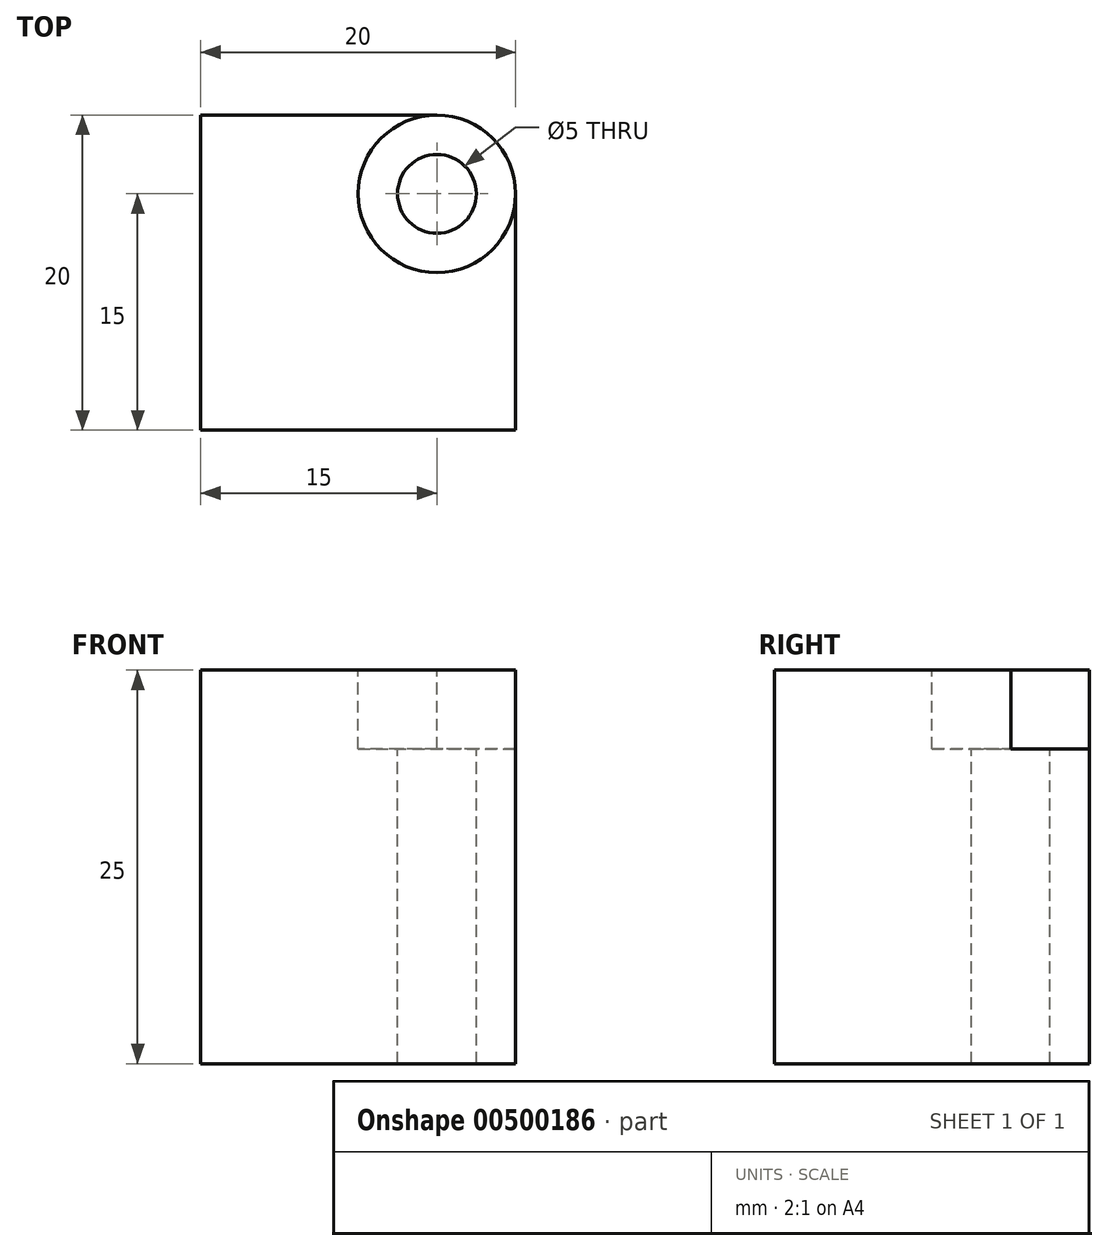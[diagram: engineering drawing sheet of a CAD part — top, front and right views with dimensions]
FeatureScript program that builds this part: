
annotation { "Feature Type Name" : "Feature", "Feature Type Description" : "" }
export const myFeature = defineFeature(function(context is Context, id is Id, definition is map)
    precondition{}
    {
        {
            var Q0;
            Q0=qCreatedBy(makeId("Top.planeOp"),FACE);
            var sketch = newSketch(context, id + "F0", { "sketchPlane" : qUnion([Q0])});
            skLineSegment(sketch, "E0", {"start": v(-68, 40) * mm, "end": v(-68, 20) * mm});
            skLineSegment(sketch, "E1", {"start": v(-68, 20) * mm, "end": v(-48, 20) * mm});
            skLineSegment(sketch, "E2", {"start": v(-68, 40) * mm, "end": v(-53, 40) * mm});
            skLineSegment(sketch, "E3", {"start": v(-48, 35) * mm, "end": v(-48, 20) * mm});
            skLineSegment(sketch, "E4", {"start": v(0, 20) * mm, "end": v(44, 20) * mm});
            skPoint(sketch, "E5.visualSharp", {"position": v(-48, 40) * mm});
            skArc(sketch, "E5.filletArc", {"start": v(-48, 35) * mm, "mid": v(-49.46, 38.54) * mm, "end": v(-53, 40) * mm});
            skSolve(sketch);
        }
        {
            var Q0;
            Q0=makeQuery(id+"F0.imprint","IMPRINT",FACE,{"disambiguationData":[TD([[makeQuery(id+"F0.imprint","IMPRINT",EDGE,{"derivedFrom":sQuery(id+"F0.wireOp",EDGE,"E0")}),1.0]])]});
            extrude(context, id + "F1", {"entities" : qUnion([Q0]), "oppositeDirection" : true, "depth" : 25 * mm});
        }
        {
            var Q0;
            Q0=sQuery(id+"F0.wireOp",VERTEX,"E5.filletArc.center");
            var Q1;
            Q1=makeQuery(id+"F1.opExtrude","SWEPT_BODY",BODY,{"disambiguationData":[OSD([sQuery(id+"F0.wireOp",EDGE,"E0"),sQuery(id+"F0.wireOp",EDGE,"E1"),sQuery(id+"F0.wireOp",EDGE,"E2"),sQuery(id+"F0.wireOp",EDGE,"E3"),sQuery(id+"F0.wireOp",EDGE,"E5.filletArc")])]});
            hole(context, id + "F2", {"style" : HoleStyle.C_BORE, "endStyle" : HoleEndStyle.THROUGH, "holeDiameter" : 5 * mm, "cBoreDiameter" : 10 * mm, "cBoreDepth" : 5 * mm, "isTappedThrough" : true, "tappedDepth" : 12 * mm, "tapClearance" : 3, "startFromSketch" : true, "locations" : qUnion([Q0]), "scope" : qUnion([Q1])});
        }
    });
